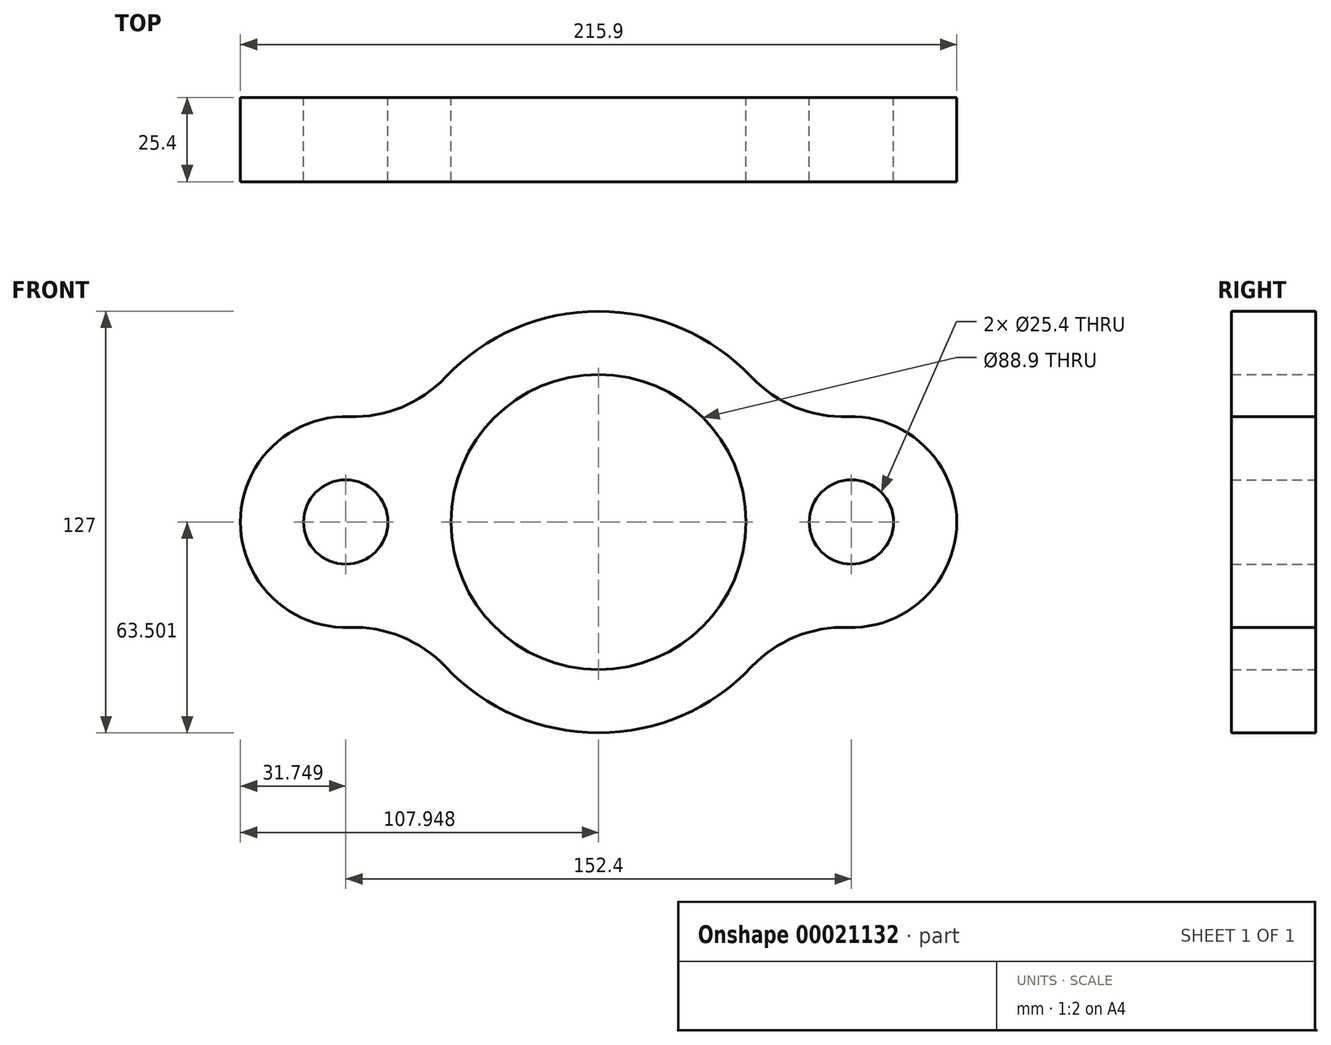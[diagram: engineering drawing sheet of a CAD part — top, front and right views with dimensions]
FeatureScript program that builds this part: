
annotation { "Feature Type Name" : "Feature", "Feature Type Description" : "" }
export const myFeature = defineFeature(function(context is Context, id is Id, definition is map)
    precondition{}
    {
        {
            var Q0;
            Q0=qCreatedBy(makeId("Front.planeOp"),FACE);
            var sketch = newSketch(context, id + "F0", { "sketchPlane" : qUnion([Q0])});
            skCircle(sketch, "E0", {"center": v(-44.2, -6.93) * mm, "radius": 44.45 * mm});
            skCircle(sketch, "E1", {"center": v(-120.4, -6.93) * mm, "radius": 12.7 * mm});
            skCircle(sketch, "E2", {"center": v(32, -6.93) * mm, "radius": 12.7 * mm});
            skCircle(sketch, "E3", {"center": v(-44.2, -6.93) * mm, "radius": 63.5 * mm});
            skCircle(sketch, "E4", {"center": v(-120.4, -6.93) * mm, "radius": 31.75 * mm});
            skCircle(sketch, "E5", {"center": v(32, -6.93) * mm, "radius": 31.75 * mm});
            skArc(sketch, "E6", {"start": v(-119.32, 24.8) * mm, "mid": v(-103.55, 27.64) * mm, "end": v(-90.34, 36.7) * mm});
            skArc(sketch, "E7", {"start": v(-90.34, -50.56) * mm, "mid": v(-103.55, -41.5) * mm, "end": v(-119.32, -38.66) * mm});
            skArc(sketch, "E8", {"start": v(1.94, 36.7) * mm, "mid": v(15.15, 27.64) * mm, "end": v(30.92, 24.8) * mm});
            skArc(sketch, "E9", {"start": v(30.92, -38.66) * mm, "mid": v(15.15, -41.5) * mm, "end": v(1.94, -50.56) * mm});
            skSolve(sketch);
        }
        {
            var Q0;
            Q0 = qSketchRegion(id + "F0", true);
            var Q1;
            {var subQ1=sQuery(id+"F0.wireOp",EDGE,"E3");var subQ5=makeQuery(id+"F0.imprint","INTERSECT",VERTEX,{"derivedFrom":[sQuery(id+"F0.wireOp",EDGE,"E1"),subQ1]});Q1=makeQuery(id+"F0.imprint","IMPRINT",FACE,{"disambiguationData":[TD([[makeQuery(id+"F0.imprint","IMPRINT",EDGE,{"disambiguationData":[TD([[subQ5,1.0]])],"derivedFrom":subQ1}),1.0]])]});}
            var Q2;
            {var subQ1=sQuery(id+"F0.wireOp",EDGE,"E3");var subQ5=makeQuery(id+"F0.imprint","INTERSECT",VERTEX,{"derivedFrom":[sQuery(id+"F0.wireOp",EDGE,"E2"),subQ1]});Q2=makeQuery(id+"F0.imprint","IMPRINT",FACE,{"disambiguationData":[TD([[makeQuery(id+"F0.imprint","IMPRINT",EDGE,{"disambiguationData":[TD([[subQ5,-1.0]])],"derivedFrom":subQ1}),1.0]])]});}
            extrude(context, id + "F1", {"entities" : qUnion([Q0, Q1, Q2]), "depth" : 25.4 * mm});
        }
    });
